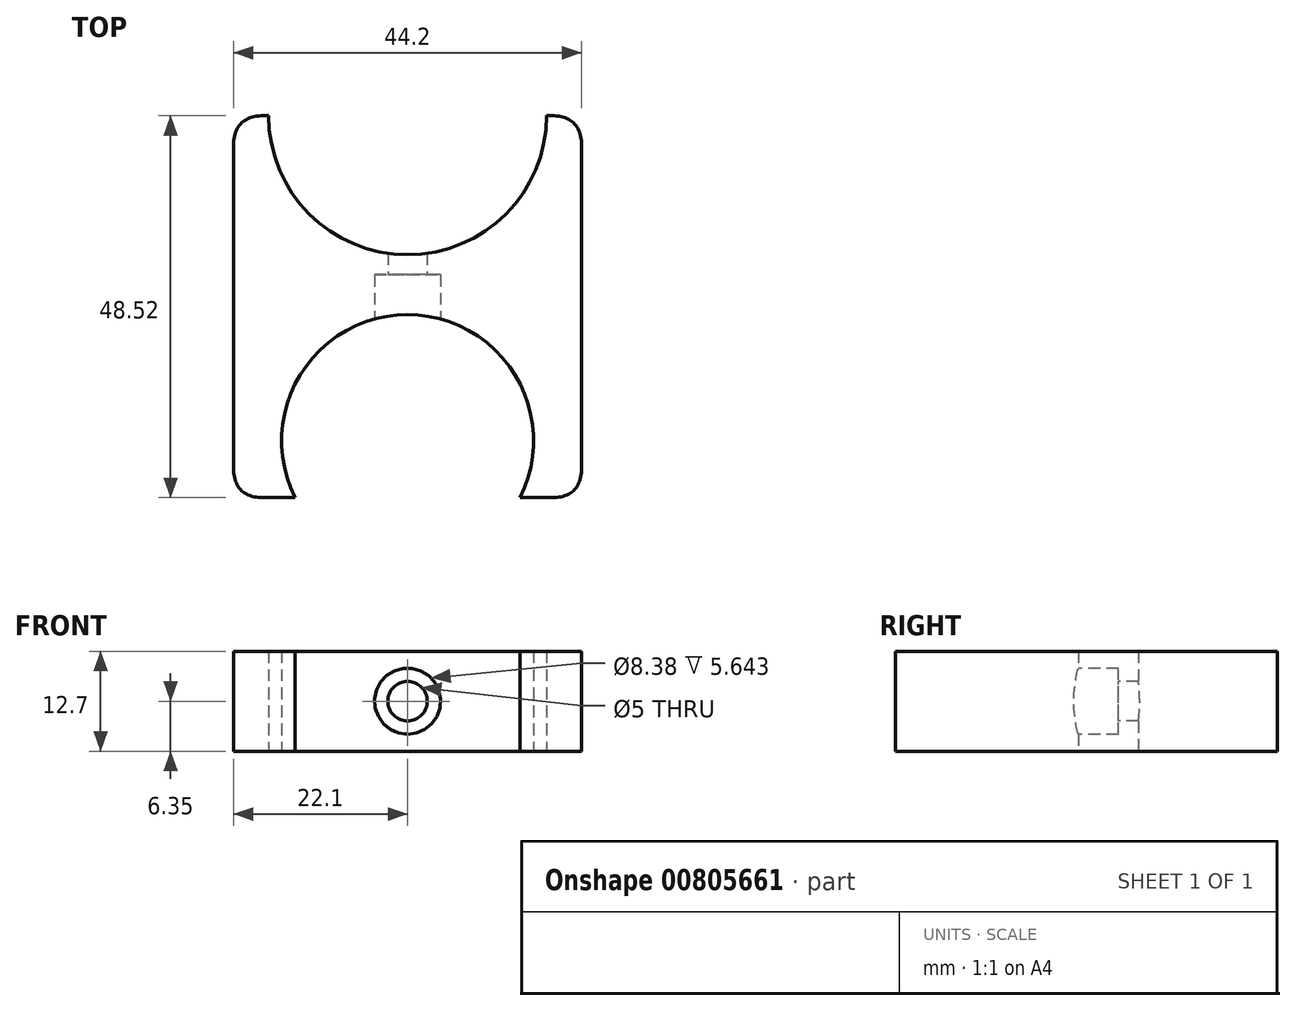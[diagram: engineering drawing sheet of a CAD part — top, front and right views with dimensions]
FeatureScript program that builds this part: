
annotation { "Feature Type Name" : "Feature", "Feature Type Description" : "" }
export const myFeature = defineFeature(function(context is Context, id is Id, definition is map)
    precondition{}
    {
        {
            var Q0;
            Q0=qCreatedBy(makeId("Top.planeOp"),FACE);
            var sketch = newSketch(context, id + "F0", { "sketchPlane" : qUnion([Q0])});
            skLineSegment(sketch, "E0.bottom", {"start": v(-22.1, 24.26) * mm, "end": v(22.1, 24.26) * mm});
            skLineSegment(sketch, "E0.top", {"start": v(-22.1, -24.26) * mm, "end": v(22.1, -24.26) * mm});
            skLineSegment(sketch, "E0.left", {"start": v(-22.1, 24.26) * mm, "end": v(-22.1, -24.26) * mm});
            skLineSegment(sketch, "E0.right", {"start": v(22.1, 24.26) * mm, "end": v(22.1, -24.26) * mm});
            skPoint(sketch, "E0.middle", {"position": v(0, 0) * mm});
            skCircle(sketch, "E1", {"center": v(0, 24.26) * mm, "radius": 17.65 * mm});
            skCircle(sketch, "E2", {"center": v(0, -17.02) * mm, "radius": 16 * mm});
            skSolve(sketch);
        }
        {
            var Q0;
            {var subQ0=sQuery(id+"F0.wireOp",EDGE,"E0.left");Q0=makeQuery(id+"F0.imprint","IMPRINT",FACE,{"disambiguationData":[TD([[makeQuery(id+"F0.imprint","IMPRINT",EDGE,{"derivedFrom":subQ0}),1.0]])]});}
            extrude(context, id + "F1", {"entities" : qUnion([Q0]), "depth" : 6.35 * mm, "offsetDistance" : 25.4 * mm, "hasSecondDirection" : true, "secondDirectionOppositeDirection" : true, "secondDirectionDepth" : 6.35 * mm});
        }
        {
            var Q0;
            Q0=qCreatedBy(makeId("Front.planeOp"),FACE);
            var sketch = newSketch(context, id + "F2", { "sketchPlane" : qUnion([Q0])});
            skCircle(sketch, "E3", {"center": v(0, 0) * mm, "radius": 4.2 * mm});
            skCircle(sketch, "E4", {"center": v(0, 0) * mm, "radius": 2.5 * mm});
            skSolve(sketch);
        }
        {
            var Q0;
            Q0=makeQuery(id+"F2.imprint","IMPRINT",FACE,{"disambiguationData":[TD([[makeQuery(id+"F2.imprint","IMPRINT",EDGE,{"derivedFrom":sQuery(id+"F2.wireOp",EDGE,"E4")}),1.0]])]});
            var Q1;
            Q1=makeQuery(id+"F2.imprint","IMPRINT",FACE,{"disambiguationData":[TD([[makeQuery(id+"F2.imprint","IMPRINT",EDGE,{"derivedFrom":sQuery(id+"F2.wireOp",EDGE,"E3")}),1.0]])]});
            var Q2;
            Q2=makeQuery(id+"F2.imprint","IMPRINT",FACE,{"disambiguationData":[TD([[makeQuery(id+"F2.imprint","IMPRINT",EDGE,{"derivedFrom":sQuery(id+"F2.wireOp",EDGE,"FrVKIAAN-Fgwa-95L2-PmD1-pfTcXxTXgpEJ")}),1.0]])]});
            var Q3;
            Q3=makeQuery(id+"F2.imprint","IMPRINT",FACE,{"disambiguationData":[TD([[makeQuery(id+"F2.imprint","IMPRINT",EDGE,{"derivedFrom":sQuery(id+"F2.wireOp",EDGE,"AU2aotcu-rxOh-S1cB-IbhK-tc6P2QUhto4p")}),1.0]])]});
            var Q4;
            Q4=sQuery(id+"F2.wireOp",EDGE,"E3");
            var Q5;
            Q5=sQuery(id+"F2.wireOp",EDGE,"E4");
            var Q6;
            Q6=sQuery(id+"F2.wireOp",EDGE,"FrVKIAAN-Fgwa-95L2-PmD1-pfTcXxTXgpEJ");
            var Q7;
            Q7=sQuery(id+"F2.wireOp",EDGE,"AU2aotcu-rxOh-S1cB-IbhK-tc6P2QUhto4p");
            extrude(context, id + "F3", {"entities" : qUnion([Q0, Q1, Q2, Q3]), "operationType" : NewBodyOperationType.REMOVE, "surfaceEntities" : qUnion([Q4, Q5, Q6, Q7]), "oppositeDirection" : true, "depth" : 4.06 * mm, "offsetDistance" : 25.4 * mm, "hasSecondDirection" : true, "secondDirectionBound" : SecondDirectionBoundingType.THROUGH_ALL, "secondDirectionOppositeDirection" : false, "secondDirectionDepth" : 25.4 * mm});
        }
        {
            var Q0;
            Q0=makeQuery(id+"F2.imprint","IMPRINT",FACE,{"disambiguationData":[TD([[makeQuery(id+"F2.imprint","IMPRINT",EDGE,{"derivedFrom":sQuery(id+"F2.wireOp",EDGE,"E4")}),1.0]])]});
            var Q1;
            Q1=makeQuery(id+"F2.imprint","IMPRINT",FACE,{"disambiguationData":[TD([[makeQuery(id+"F2.imprint","IMPRINT",EDGE,{"derivedFrom":sQuery(id+"F2.wireOp",EDGE,"FrVKIAAN-Fgwa-95L2-PmD1-pfTcXxTXgpEJ")}),1.0]])]});
            var Q2;
            Q2=sQuery(id+"F2.wireOp",EDGE,"E4");
            var Q3;
            Q3=sQuery(id+"F2.wireOp",EDGE,"FrVKIAAN-Fgwa-95L2-PmD1-pfTcXxTXgpEJ");
            extrude(context, id + "F4", {"entities" : qUnion([Q0, Q1]), "operationType" : NewBodyOperationType.REMOVE, "surfaceEntities" : qUnion([Q2, Q3]), "endBound" : BoundingType.THROUGH_ALL, "oppositeDirection" : true, "depth" : 6.35 * mm, "offsetDistance" : 25.4 * mm});
        }
        {
            var Q0;
            Q0=makeQuery(id+"F1.opExtrude","SWEPT_EDGE",EDGE,{"disambiguationData":[OSD([sQuery(id+"F0.wireOp",EDGE,"E0.top"),sQuery(id+"F0.wireOp",EDGE,"E0.left")])]});
            var Q1;
            Q1=makeQuery(id+"F1.opExtrude","SWEPT_EDGE",EDGE,{"disambiguationData":[OSD([sQuery(id+"F0.wireOp",EDGE,"E0.top"),sQuery(id+"F0.wireOp",EDGE,"E0.right")])]});
            var Q2;
            Q2=makeQuery(id+"F1.opExtrude","SWEPT_EDGE",EDGE,{"disambiguationData":[OSD([sQuery(id+"F0.wireOp",EDGE,"E0.bottom"),sQuery(id+"F0.wireOp",EDGE,"E0.left")])]});
            var Q3;
            Q3=makeQuery(id+"F1.opExtrude","SWEPT_EDGE",EDGE,{"disambiguationData":[OSD([sQuery(id+"F0.wireOp",EDGE,"E0.bottom"),sQuery(id+"F0.wireOp",EDGE,"E0.right")])]});
            fillet(context, id + "F5", {"entities" : qUnion([Q0, Q1, Q2, Q3]), "radius" : 3.8 * mm, "tangentPropagation" : true, "rho" : 0.5, "crossSection" : FilletCrossSection.CONIC, "allowEdgeOverflow" : false});
        }
    });
